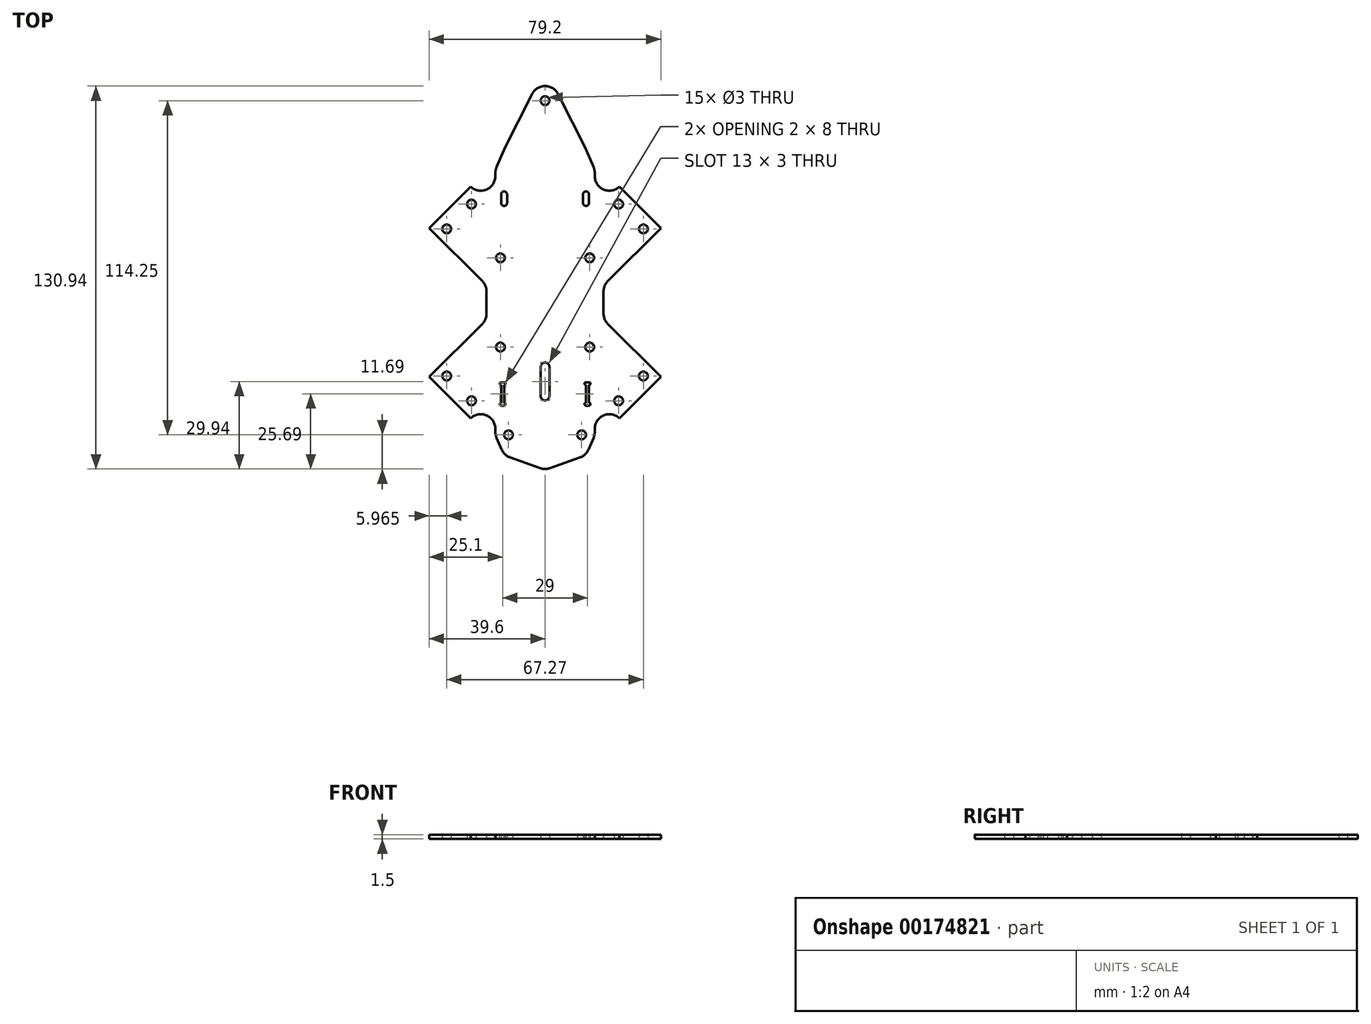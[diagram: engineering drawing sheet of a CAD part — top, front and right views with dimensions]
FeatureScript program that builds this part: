
annotation { "Feature Type Name" : "Feature", "Feature Type Description" : "" }
export const myFeature = defineFeature(function(context is Context, id is Id, definition is map)
    precondition{}
    {
        {
            var Q0;
            Q0=qCreatedBy(makeId("Top.planeOp"),FACE);
            var sketch = newSketch(context, id + "F0", { "sketchPlane" : qUnion([Q0])});
            skLineSegment(sketch, "E0.bottom", {"start": v(-15.25, 15.25) * mm, "end": v(15.25, 15.25) * mm, "construction": true});
            skLineSegment(sketch, "E0.top", {"start": v(-15.25, -15.25) * mm, "end": v(15.25, -15.25) * mm, "construction": true});
            skLineSegment(sketch, "E0.left", {"start": v(-15.25, 15.25) * mm, "end": v(-15.25, -15.25) * mm, "construction": true});
            skLineSegment(sketch, "E0.right", {"start": v(15.25, 15.25) * mm, "end": v(15.25, -15.25) * mm, "construction": true});
            skLineSegment(sketch, "E1", {"start": v(0, 0) * mm, "end": v(-74.25, 74.25) * mm, "construction": true});
            skLineSegment(sketch, "E2", {"start": v(0, 0) * mm, "end": v(74.25, 74.25) * mm, "construction": true});
            skLineSegment(sketch, "E3", {"start": v(0, 0) * mm, "end": v(74.25, -74.25) * mm, "construction": true});
            skLineSegment(sketch, "E4", {"start": v(0, 0) * mm, "end": v(-74.25, -74.25) * mm, "construction": true});
            skCircle(sketch, "E5", {"center": v(74.25, 74.25) * mm, "radius": 63.5 * mm, "construction": true});
            skCircle(sketch, "E6", {"center": v(-74.25, 74.25) * mm, "radius": 63.5 * mm, "construction": true});
            skCircle(sketch, "E7", {"center": v(-74.25, -74.25) * mm, "radius": 63.5 * mm, "construction": true});
            skCircle(sketch, "E8", {"center": v(74.25, -74.25) * mm, "radius": 63.5 * mm, "construction": true});
            skCircle(sketch, "E9", {"center": v(0, 0) * mm, "radius": 105 * mm, "construction": true});
            skCircle(sketch, "E10", {"center": v(-15.25, 15.25) * mm, "radius": 1.5 * mm});
            skCircle(sketch, "E11", {"center": v(-15.25, -15.25) * mm, "radius": 1.5 * mm});
            skCircle(sketch, "E12", {"center": v(15.25, -15.25) * mm, "radius": 1.5 * mm});
            skCircle(sketch, "E13", {"center": v(15.25, 15.25) * mm, "radius": 1.5 * mm});
            skLineSegment(sketch, "E14", {"start": v(-39.6, 25.46) * mm, "end": v(-25.46, 39.6) * mm});
            skLineSegment(sketch, "E15", {"start": v(-25.46, 39.6) * mm, "end": v(-17, 31.14) * mm});
            skLineSegment(sketch, "E16", {"start": v(39.6, -25.46) * mm, "end": v(25.46, -39.6) * mm});
            skLineSegment(sketch, "E17", {"start": v(25.46, -39.6) * mm, "end": v(17, -31.14) * mm});
            skLineSegment(sketch, "E18", {"start": v(-39.6, -25.46) * mm, "end": v(-20, -5.86) * mm});
            skLineSegment(sketch, "E19", {"start": v(25.46, 39.6) * mm, "end": v(39.6, 25.46) * mm});
            skLineSegment(sketch, "E20", {"start": v(39.6, 25.46) * mm, "end": v(20, 5.86) * mm});
            skLineSegment(sketch, "E21", {"start": v(-25.46, -39.6) * mm, "end": v(-39.6, -25.46) * mm});
            skLineSegment(sketch, "E22.trimOffspring", {"start": v(17, 31.14) * mm, "end": v(25.46, 39.6) * mm});
            skLineSegment(sketch, "E23.trimOffspring", {"start": v(-17, -31.14) * mm, "end": v(-25.46, -39.6) * mm});
            skLineSegment(sketch, "E24.trimOffspring", {"start": v(-20, 5.86) * mm, "end": v(-39.6, 25.46) * mm});
            skLineSegment(sketch, "E25.trimOffspring", {"start": v(20, -5.86) * mm, "end": v(39.6, -25.46) * mm});
            skLineSegment(sketch, "E26", {"start": v(-20, 5.86) * mm, "end": v(-20, -5.86) * mm});
            skLineSegment(sketch, "E27", {"start": v(20, 5.86) * mm, "end": v(20, -5.86) * mm});
            skCircle(sketch, "E28", {"center": v(-12.5, -45.25) * mm, "radius": 1.5 * mm});
            skCircle(sketch, "E29", {"center": v(12.5, -45.25) * mm, "radius": 1.5 * mm});
            skLineSegment(sketch, "E30", {"start": v(-17, -31.14) * mm, "end": v(-17, -45.25) * mm});
            skLineSegment(sketch, "E31", {"start": v(17, -31.14) * mm, "end": v(17, -45.25) * mm});
            skLineSegment(sketch, "E32", {"start": v(17, -45.25) * mm, "end": v(14, -52.25) * mm});
            skLineSegment(sketch, "E33", {"start": v(-17, -45.25) * mm, "end": v(-14, -52.25) * mm});
            skLineSegment(sketch, "E34", {"start": v(-14, -52.25) * mm, "end": v(0, -57.25) * mm});
            skLineSegment(sketch, "E35", {"start": v(0, -57.25) * mm, "end": v(14, -52.25) * mm});
            skCircle(sketch, "E36", {"center": v(-33.63, 25.15) * mm, "radius": 1.5 * mm});
            skCircle(sketch, "E37", {"center": v(-25.15, 33.63) * mm, "radius": 1.5 * mm});
            skCircle(sketch, "E38", {"center": v(25.15, 33.63) * mm, "radius": 1.5 * mm});
            skCircle(sketch, "E39", {"center": v(33.63, 25.15) * mm, "radius": 1.5 * mm});
            skCircle(sketch, "E40", {"center": v(25.15, -33.63) * mm, "radius": 1.5 * mm});
            skCircle(sketch, "E41", {"center": v(33.63, -25.15) * mm, "radius": 1.5 * mm});
            skCircle(sketch, "E42", {"center": v(-33.63, -25.15) * mm, "radius": 1.5 * mm});
            skCircle(sketch, "E43", {"center": v(-25.15, -33.63) * mm, "radius": 1.5 * mm});
            skLineSegment(sketch, "E44", {"start": v(-33.63, -25.15) * mm, "end": v(-25.15, -33.63) * mm, "construction": true});
            skLineSegment(sketch, "E45", {"start": v(25.15, -33.63) * mm, "end": v(33.63, -25.15) * mm, "construction": true});
            skLineSegment(sketch, "E46", {"start": v(33.63, 25.15) * mm, "end": v(25.15, 33.63) * mm, "construction": true});
            skLineSegment(sketch, "E47", {"start": v(-25.15, 33.63) * mm, "end": v(-33.63, 25.15) * mm, "construction": true});
            skLineSegment(sketch, "E48", {"start": v(-17, 31.14) * mm, "end": v(-17, 45.25) * mm});
            skLineSegment(sketch, "E49", {"start": v(-17, 45.25) * mm, "end": v(-14, 52.25) * mm});
            skLineSegment(sketch, "E50", {"start": v(17, 31.14) * mm, "end": v(17, 45.25) * mm});
            skLineSegment(sketch, "E51", {"start": v(17, 45.25) * mm, "end": v(14, 52.25) * mm});
            skLineSegment(sketch, "E52", {"start": v(-14, 52.25) * mm, "end": v(-4.47, 71.24) * mm});
            skLineSegment(sketch, "E53", {"start": v(4.47, 71.24) * mm, "end": v(14, 52.25) * mm});
            skCircle(sketch, "E54", {"center": v(0, 69) * mm, "radius": 1.5 * mm});
            skPoint(sketch, "E55.visualSharp", {"position": v(0, 80.15) * mm});
            skArc(sketch, "E55.filletArc", {"start": v(4.47, 71.24) * mm, "mid": v(0, 74) * mm, "end": v(-4.47, 71.24) * mm});
            skArc(sketch, "E56", {"start": v(1.5, -22) * mm, "mid": v(0, -20.5) * mm, "end": v(-1.5, -22) * mm});
            skArc(sketch, "E57", {"start": v(-1.5, -32) * mm, "mid": v(0, -33.5) * mm, "end": v(1.5, -32) * mm});
            skLineSegment(sketch, "E58", {"start": v(-1.5, -22) * mm, "end": v(-1.5, -32) * mm});
            skLineSegment(sketch, "E59", {"start": v(1.5, -32) * mm, "end": v(1.5, -22) * mm});
            skArc(sketch, "E60", {"start": v(15, 37) * mm, "mid": v(14, 38) * mm, "end": v(13, 37) * mm});
            skArc(sketch, "E61", {"start": v(13, 34) * mm, "mid": v(14, 33) * mm, "end": v(15, 34) * mm});
            skLineSegment(sketch, "E62", {"start": v(14, 37) * mm, "end": v(14, 34) * mm, "construction": true});
            skLineSegment(sketch, "E63", {"start": v(15, 37) * mm, "end": v(15, 34) * mm});
            skLineSegment(sketch, "E64", {"start": v(13, 37) * mm, "end": v(13, 34) * mm});
            skArc(sketch, "E65.MirrorCS", {"start": v(-15, 37) * mm, "mid": v(-14, 38) * mm, "end": v(-13, 37) * mm});
            skLineSegment(sketch, "E66.MirrorCS", {"start": v(-14, 37) * mm, "end": v(-14, 34) * mm, "construction": true});
            skArc(sketch, "E67.MirrorCS", {"start": v(-13, 34) * mm, "mid": v(-14, 33) * mm, "end": v(-15, 34) * mm});
            skLineSegment(sketch, "E68.MirrorCS", {"start": v(-15, 37) * mm, "end": v(-15, 34) * mm});
            skLineSegment(sketch, "E69.MirrorCS", {"start": v(-13, 37) * mm, "end": v(-13, 34) * mm});
            skSolve(sketch);
        }
        {
            var Q0;
            Q0=qSketchRegion(id+"F0",true);
            extrude(context, id + "F1", {"entities" : qUnion([Q0]), "depth" : 1.5 * mm});
        }
        {
            var Q0;
            Q0=makeQuery(id+"F1.opExtrude","SWEPT_EDGE",EDGE,{"disambiguationData":[OSD([sQuery(id+"F0.wireOp",EDGE,"E17"),sQuery(id+"F0.wireOp",EDGE,"E31")])]});
            var Q1;
            Q1=makeQuery(id+"F1.opExtrude","SWEPT_EDGE",EDGE,{"disambiguationData":[OSD([sQuery(id+"F0.wireOp",EDGE,"E23.trimOffspring"),sQuery(id+"F0.wireOp",EDGE,"E30")])]});
            var Q2;
            Q2=makeQuery(id+"F1.opExtrude","SWEPT_EDGE",EDGE,{"disambiguationData":[OSD([sQuery(id+"F0.wireOp",EDGE,"E15"),sQuery(id+"F0.wireOp",EDGE,"E48")])]});
            var Q3;
            Q3=makeQuery(id+"F1.opExtrude","SWEPT_EDGE",EDGE,{"disambiguationData":[OSD([sQuery(id+"F0.wireOp",EDGE,"E22.trimOffspring"),sQuery(id+"F0.wireOp",EDGE,"E50")])]});
            fillet(context, id + "F2", {"entities" : qUnion([Q0, Q1, Q2, Q3]), "radius" : 5 * mm, "tangentPropagation" : true, "allowEdgeOverflow" : false});
        }
        {
            var Q0;
            Q0=makeQuery(id+"F1.opExtrude","SWEPT_EDGE",EDGE,{"disambiguationData":[OSD([sQuery(id+"F0.wireOp",EDGE,"E20"),sQuery(id+"F0.wireOp",EDGE,"E27")])]});
            var Q1;
            Q1=makeQuery(id+"F1.opExtrude","SWEPT_EDGE",EDGE,{"disambiguationData":[OSD([sQuery(id+"F0.wireOp",EDGE,"E25.trimOffspring"),sQuery(id+"F0.wireOp",EDGE,"E27")])]});
            var Q2;
            Q2=makeQuery(id+"F1.opExtrude","SWEPT_EDGE",EDGE,{"disambiguationData":[OSD([sQuery(id+"F0.wireOp",EDGE,"E18"),sQuery(id+"F0.wireOp",EDGE,"E26")])]});
            var Q3;
            Q3=makeQuery(id+"F1.opExtrude","SWEPT_EDGE",EDGE,{"disambiguationData":[OSD([sQuery(id+"F0.wireOp",EDGE,"E24.trimOffspring"),sQuery(id+"F0.wireOp",EDGE,"E26")])]});
            var Q4;
            Q4=makeQuery(id+"F1.opExtrude","SWEPT_EDGE",EDGE,{"disambiguationData":[OSD([sQuery(id+"F0.wireOp",EDGE,"E31"),sQuery(id+"F0.wireOp",EDGE,"E32")])]});
            var Q5;
            Q5=makeQuery(id+"F1.opExtrude","SWEPT_EDGE",EDGE,{"disambiguationData":[OSD([sQuery(id+"F0.wireOp",EDGE,"E32"),sQuery(id+"F0.wireOp",EDGE,"E35")])]});
            var Q6;
            Q6=makeQuery(id+"F1.opExtrude","SWEPT_EDGE",EDGE,{"disambiguationData":[OSD([sQuery(id+"F0.wireOp",EDGE,"E34"),sQuery(id+"F0.wireOp",EDGE,"E35")])]});
            var Q7;
            Q7=makeQuery(id+"F1.opExtrude","SWEPT_EDGE",EDGE,{"disambiguationData":[OSD([sQuery(id+"F0.wireOp",EDGE,"E33"),sQuery(id+"F0.wireOp",EDGE,"E34")])]});
            var Q8;
            Q8=makeQuery(id+"F1.opExtrude","SWEPT_EDGE",EDGE,{"disambiguationData":[OSD([sQuery(id+"F0.wireOp",EDGE,"E30"),sQuery(id+"F0.wireOp",EDGE,"E33")])]});
            var Q9;
            Q9=makeQuery(id+"F1.opExtrude","SWEPT_EDGE",EDGE,{"disambiguationData":[OSD([sQuery(id+"F0.wireOp",EDGE,"E48"),sQuery(id+"F0.wireOp",EDGE,"E49")])]});
            var Q10;
            Q10=makeQuery(id+"F1.opExtrude","SWEPT_EDGE",EDGE,{"disambiguationData":[OSD([sQuery(id+"F0.wireOp",EDGE,"E49"),sQuery(id+"F0.wireOp",EDGE,"E52")])]});
            var Q11;
            Q11=makeQuery(id+"F1.opExtrude","SWEPT_EDGE",EDGE,{"disambiguationData":[OSD([sQuery(id+"F0.wireOp",EDGE,"E51"),sQuery(id+"F0.wireOp",EDGE,"E53")])]});
            var Q12;
            Q12=makeQuery(id+"F1.opExtrude","SWEPT_EDGE",EDGE,{"disambiguationData":[OSD([sQuery(id+"F0.wireOp",EDGE,"E50"),sQuery(id+"F0.wireOp",EDGE,"E51")])]});
            fillet(context, id + "F3", {"entities" : qUnion([Q0, Q1, Q2, Q3, Q4, Q5, Q6, Q7, Q8, Q9, Q10, Q11, Q12]), "radius" : 5 * mm, "tangentPropagation" : true, "allowEdgeOverflow" : false});
        }
        {
            var Q0;
            Q0=makeQuery(id+"F1.opExtrude","CAP_FACE",FACE,{"disambiguationData":[OSD([sQuery(id+"F0.wireOp",EDGE,"E10"),sQuery(id+"F0.wireOp",EDGE,"E11"),sQuery(id+"F0.wireOp",EDGE,"E12"),sQuery(id+"F0.wireOp",EDGE,"E13"),sQuery(id+"F0.wireOp",EDGE,"E14"),sQuery(id+"F0.wireOp",EDGE,"E15"),sQuery(id+"F0.wireOp",EDGE,"E16"),sQuery(id+"F0.wireOp",EDGE,"E17"),sQuery(id+"F0.wireOp",EDGE,"E18"),sQuery(id+"F0.wireOp",EDGE,"E19"),sQuery(id+"F0.wireOp",EDGE,"E20"),sQuery(id+"F0.wireOp",EDGE,"E21"),sQuery(id+"F0.wireOp",EDGE,"E22.trimOffspring"),sQuery(id+"F0.wireOp",EDGE,"E23.trimOffspring"),sQuery(id+"F0.wireOp",EDGE,"E24.trimOffspring"),sQuery(id+"F0.wireOp",EDGE,"E25.trimOffspring"),sQuery(id+"F0.wireOp",EDGE,"E26"),sQuery(id+"F0.wireOp",EDGE,"E27"),sQuery(id+"F0.wireOp",EDGE,"E28"),sQuery(id+"F0.wireOp",EDGE,"E29"),sQuery(id+"F0.wireOp",EDGE,"E30"),sQuery(id+"F0.wireOp",EDGE,"E31"),sQuery(id+"F0.wireOp",EDGE,"E32"),sQuery(id+"F0.wireOp",EDGE,"E33"),sQuery(id+"F0.wireOp",EDGE,"E34"),sQuery(id+"F0.wireOp",EDGE,"E35"),sQuery(id+"F0.wireOp",EDGE,"E36"),sQuery(id+"F0.wireOp",EDGE,"E37"),sQuery(id+"F0.wireOp",EDGE,"E38"),sQuery(id+"F0.wireOp",EDGE,"E39"),sQuery(id+"F0.wireOp",EDGE,"E40"),sQuery(id+"F0.wireOp",EDGE,"E41"),sQuery(id+"F0.wireOp",EDGE,"E42"),sQuery(id+"F0.wireOp",EDGE,"E43"),sQuery(id+"F0.wireOp",EDGE,"E48"),sQuery(id+"F0.wireOp",EDGE,"E49"),sQuery(id+"F0.wireOp",EDGE,"E50"),sQuery(id+"F0.wireOp",EDGE,"E51"),sQuery(id+"F0.wireOp",EDGE,"E52"),sQuery(id+"F0.wireOp",EDGE,"E53"),sQuery(id+"F0.wireOp",EDGE,"E54"),sQuery(id+"F0.wireOp",EDGE,"E55.filletArc"),sQuery(id+"F0.wireOp",EDGE,"E56"),sQuery(id+"F0.wireOp",EDGE,"E57"),sQuery(id+"F0.wireOp",EDGE,"E58"),sQuery(id+"F0.wireOp",EDGE,"E59"),sQuery(id+"F0.wireOp",EDGE,"E60"),sQuery(id+"F0.wireOp",EDGE,"E61"),sQuery(id+"F0.wireOp",EDGE,"E63"),sQuery(id+"F0.wireOp",EDGE,"E64"),sQuery(id+"F0.wireOp",EDGE,"E65.MirrorCS"),sQuery(id+"F0.wireOp",EDGE,"E67.MirrorCS"),sQuery(id+"F0.wireOp",EDGE,"E68.MirrorCS"),sQuery(id+"F0.wireOp",EDGE,"E69.MirrorCS")])],"isStart":false});
            var sketch = newSketch(context, id + "F4", { "sketchPlane" : qUnion([Q0])});
            skLineSegment(sketch, "E70.bottom", {"start": v(-15, -27.25) * mm, "end": v(-14, -27.25) * mm});
            skLineSegment(sketch, "E70.top", {"start": v(-15, -35.25) * mm, "end": v(-14, -35.25) * mm});
            skLineSegment(sketch, "E70.left", {"start": v(-15, -28.25) * mm, "end": v(-15, -34.25) * mm});
            skLineSegment(sketch, "E70.right", {"start": v(-14, -28.25) * mm, "end": v(-14, -34.25) * mm});
            skArc(sketch, "E71", {"start": v(-15, -34.25) * mm, "mid": v(-15.5, -34.75) * mm, "end": v(-15, -35.25) * mm});
            skArc(sketch, "E72", {"start": v(-14, -35.25) * mm, "mid": v(-13.5, -34.75) * mm, "end": v(-14, -34.25) * mm});
            skArc(sketch, "E73", {"start": v(-15, -27.25) * mm, "mid": v(-15.5, -27.75) * mm, "end": v(-15, -28.25) * mm});
            skArc(sketch, "E74", {"start": v(-14, -28.25) * mm, "mid": v(-13.5, -27.75) * mm, "end": v(-14, -27.25) * mm});
            skArc(sketch, "E75.MirrorCS", {"start": v(15, -27.25) * mm, "mid": v(15.5, -27.75) * mm, "end": v(15, -28.25) * mm});
            skArc(sketch, "E76.MirrorCS", {"start": v(14, -28.25) * mm, "mid": v(13.5, -27.75) * mm, "end": v(14, -27.25) * mm});
            skLineSegment(sketch, "E77.MirrorCS", {"start": v(15, -27.25) * mm, "end": v(14, -27.25) * mm});
            skArc(sketch, "E78.MirrorCS", {"start": v(15, -34.25) * mm, "mid": v(15.5, -34.75) * mm, "end": v(15, -35.25) * mm});
            skLineSegment(sketch, "E79.MirrorCS", {"start": v(15, -35.25) * mm, "end": v(14, -35.25) * mm});
            skArc(sketch, "E80.MirrorCS", {"start": v(14, -35.25) * mm, "mid": v(13.5, -34.75) * mm, "end": v(14, -34.25) * mm});
            skLineSegment(sketch, "E81.MirrorCS", {"start": v(15, -28.25) * mm, "end": v(15, -34.25) * mm});
            skLineSegment(sketch, "E82.MirrorCS", {"start": v(14, -28.25) * mm, "end": v(14, -34.25) * mm});
            skSolve(sketch);
        }
        {
            var Q0;
            Q0 = qSketchRegion(id + "F4", true);
            extrude(context, id + "F5", {"entities" : qUnion([Q0]), "operationType" : NewBodyOperationType.REMOVE, "oppositeDirection" : true, "depth" : 25 * mm});
        }
    });
